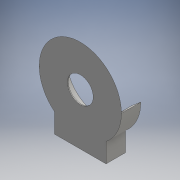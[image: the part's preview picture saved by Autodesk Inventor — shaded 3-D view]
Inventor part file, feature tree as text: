
AUTODESK INVENTOR PART (.ipt)
format: ipt  version: 2016 (Build 200138000, 138)  size: 166,912 bytes
history: native  units: mm
features: sketch x7, extrude x5, revolve x1, hole x1
ambient origin geometry x8: Origin, YZ Plane, XZ Plane, XY Plane, X Axis, Y Axis, Z Axis, Center Point
bodies: Solid1 (feature_tree)
feature tree (14):
  revolve  "Revolution1"  [1 undecoded]
  extrude  "Extrusion1"  TaperAngle=90.0deg  [1 undecoded]
  extrude  "Extrusion2"  Depth=16.0mm
  extrude  "Extrusion3"  Depth=3.0mm TaperAngle=0.0deg
  extrude  "Extrusion7"  Depth=10.0mm TaperAngle=0.0deg
  extrude  "Extrusion8"  Depth=4.35mm
  hole  "Hole2"  [1 undecoded]
  sketch  "Sketch1"  dims[d0=20.5mm d1=2.0mm]
  sketch  "Sketch2"  dims[d2=5.0mm d3=90.0deg]
  sketch  "Sketch3"  dims[d4=0.5mm d5=0.0mm d6=16.0mm]
  sketch  "Sketch4"  dims[d7=0.5mm d8=0.0mm d12=3.0mm d13=0.0mm]
  sketch  "Sketch10"  dims[d33=6.981317mm d35=10.0mm d36=0.0mm]
  sketch  "Sketch11"  dims[d37=9.0mm d38=0.0mm d39=4.35mm]
  sketch  "Sketch12"  dims[d40=6.5mm d41=4.35mm d42=6.0mm d43=6.0mm d44=4.35mm d45=6.0mm d46=4.0mm d47=2.0mm d48=90.0deg d49=8.0mm d50=20.594885mm d51=6.5mm]
note: 3 required parameter values undecoded (feature->parameter linkage not recoverable at this tier; creation-order binding heuristic only, values carry confidence <= 0.55)